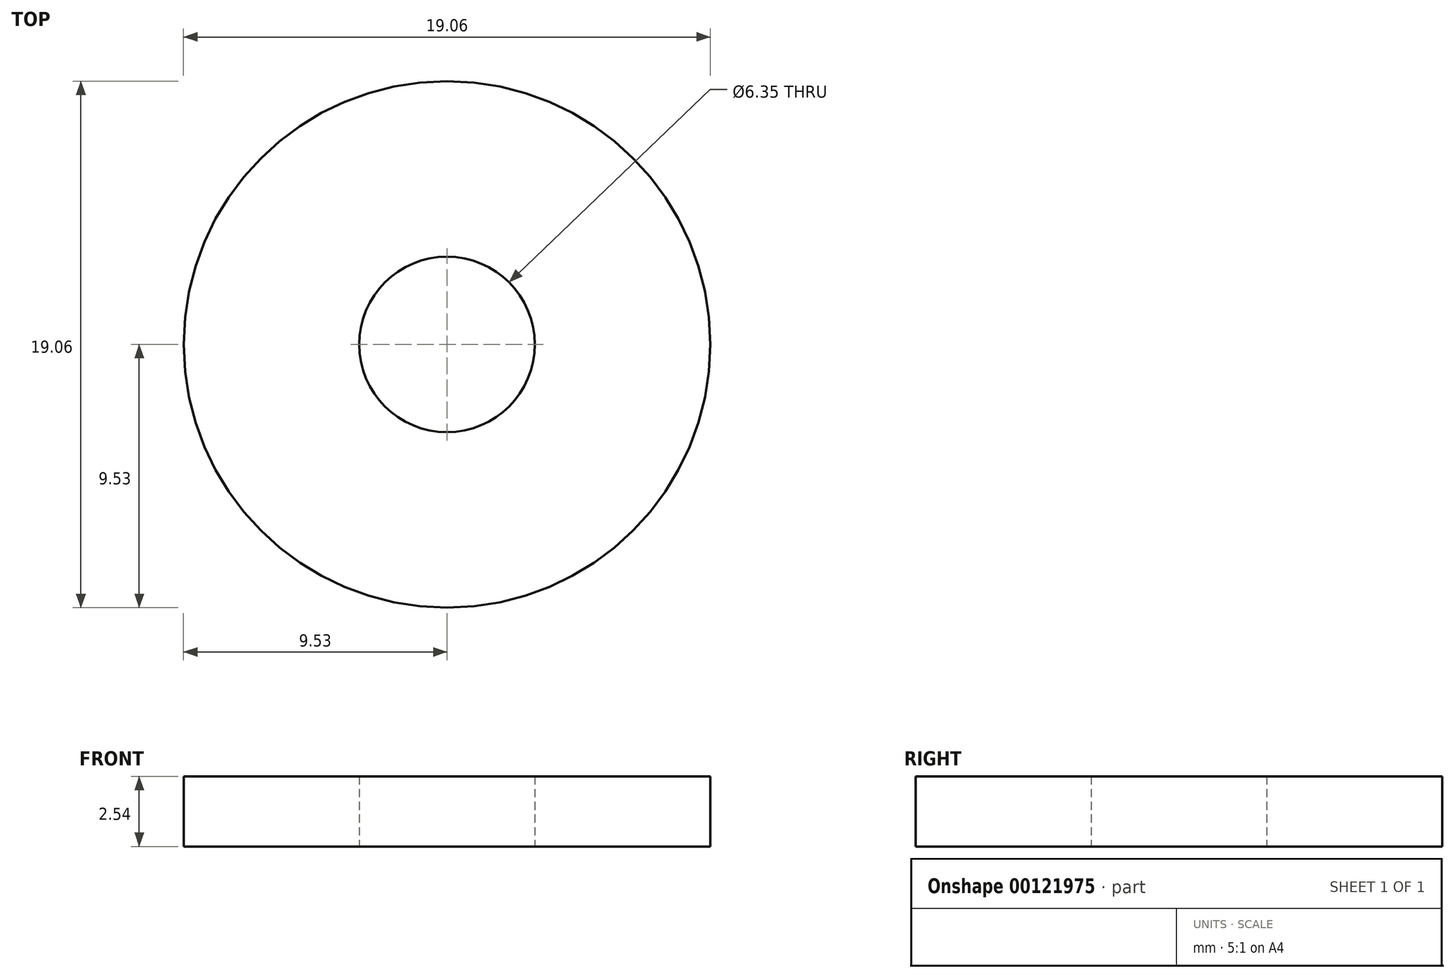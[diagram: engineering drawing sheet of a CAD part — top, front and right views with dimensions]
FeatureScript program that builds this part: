
annotation { "Feature Type Name" : "Feature", "Feature Type Description" : "" }
export const myFeature = defineFeature(function(context is Context, id is Id, definition is map)
    precondition{}
    {
        {
            var Q0;
            Q0=qCreatedBy(makeId("Top.planeOp"),FACE);
            var sketch = newSketch(context, id + "F0", { "sketchPlane" : qUnion([Q0])});
            skCircle(sketch, "E0", {"center": v(0, 0) * mm, "radius": 3.18 * mm});
            skCircle(sketch, "E1", {"center": v(0, 0) * mm, "radius": 9.53 * mm});
            skSolve(sketch);
        }
        {
            var Q0;
            Q0=makeQuery(id+"F0.imprint","IMPRINT",FACE,{"disambiguationData":[TD([[makeQuery(id+"F0.imprint","IMPRINT",EDGE,{"derivedFrom":sQuery(id+"F0.wireOp",EDGE,"E0")}),-1.0]])]});
            extrude(context, id + "F1", {"entities" : qUnion([Q0]), "depth" : 2.54 * mm});
        }
    });
